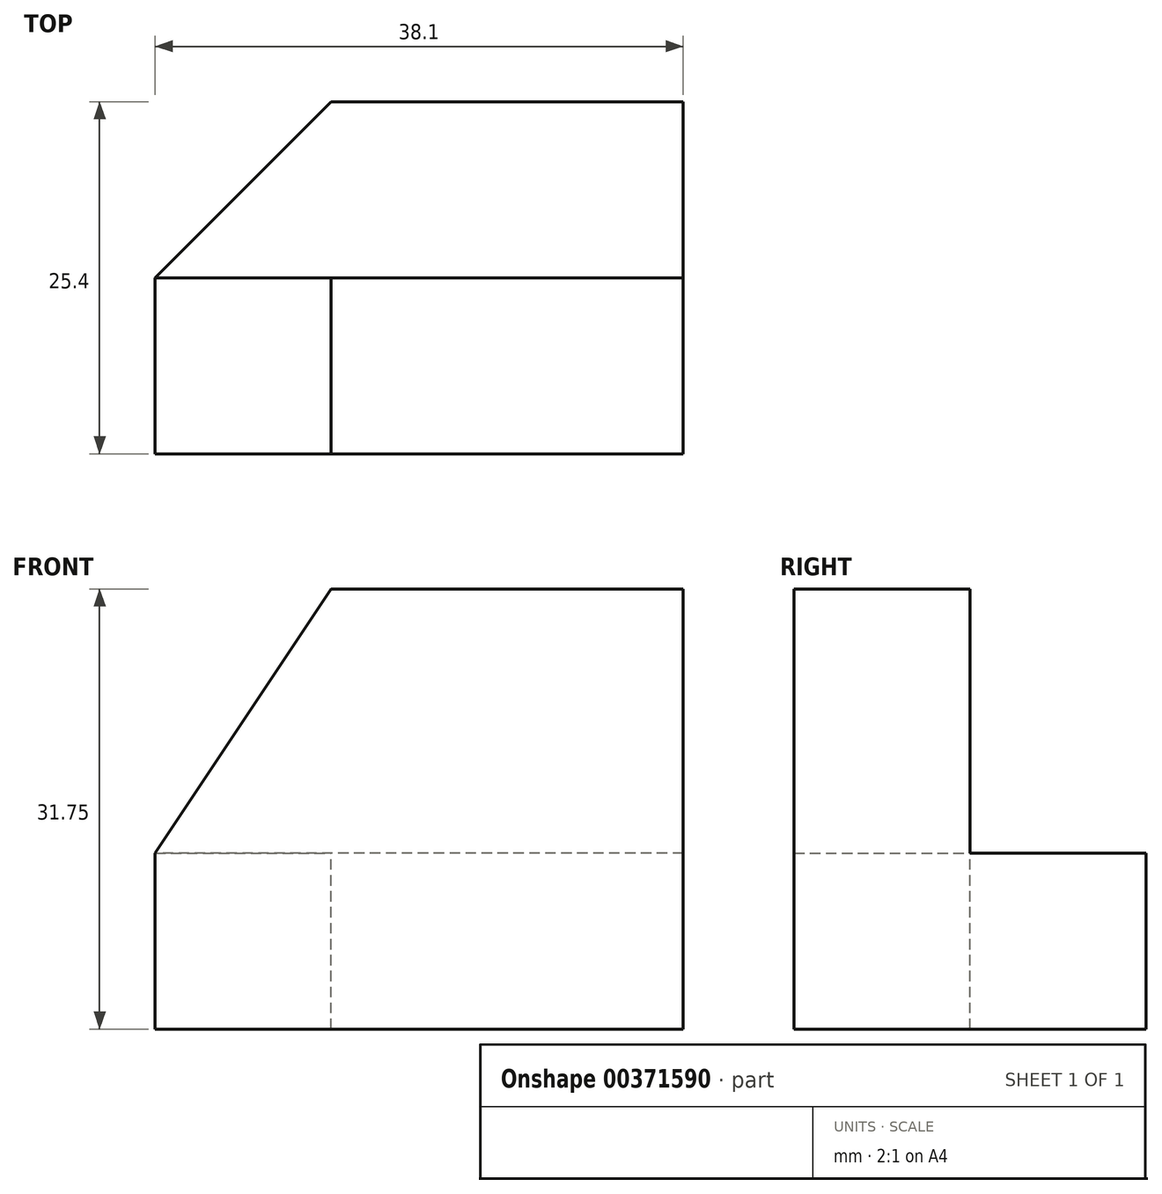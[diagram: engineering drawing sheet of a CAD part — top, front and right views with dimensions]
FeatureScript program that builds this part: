
annotation { "Feature Type Name" : "Feature", "Feature Type Description" : "" }
export const myFeature = defineFeature(function(context is Context, id is Id, definition is map)
    precondition{}
    {
        {
            var Q0;
            Q0=qCreatedBy(makeId("Right.planeOp"),FACE);
            var sketch = newSketch(context, id + "F0", { "sketchPlane" : qUnion([Q0])});
            skLineSegment(sketch, "E0.bottom", {"start": v(0, 0) * mm, "end": v(25.4, 0) * mm});
            skLineSegment(sketch, "E0.top", {"start": v(0, 31.75) * mm, "end": v(25.4, 31.75) * mm});
            skLineSegment(sketch, "E0.left", {"start": v(0, 0) * mm, "end": v(0, 31.75) * mm});
            skLineSegment(sketch, "E0.right", {"start": v(25.4, 0) * mm, "end": v(25.4, 31.75) * mm});
            skSolve(sketch);
        }
        {
            var Q0;
            Q0 = qSketchRegion(id + "F0", true);
            extrude(context, id + "F1", {"entities" : qUnion([Q0]), "depth" : 38.1 * mm});
        }
        {
            var Q0;
            Q0=makeQuery(id+"F1.opExtrude","CAP_FACE",FACE,{"disambiguationData":[OSD([sQuery(id+"F0.wireOp",EDGE,"E0.bottom"),sQuery(id+"F0.wireOp",EDGE,"E0.top"),sQuery(id+"F0.wireOp",EDGE,"E0.left"),sQuery(id+"F0.wireOp",EDGE,"E0.right")])],"isStart":true});
            var sketch = newSketch(context, id + "F2", { "sketchPlane" : qUnion([Q0])});
            skLineSegment(sketch, "E1", {"start": v(-12.7, 31.75) * mm, "end": v(-12.7, 12.7) * mm});
            skLineSegment(sketch, "E2", {"start": v(-12.7, 12.7) * mm, "end": v(-25.4, 12.7) * mm});
            skSolve(sketch);
        }
        {
            var Q0;
            {var subQ0=sQuery(id+"F2.wireOp",EDGE,"E1");Q0=makeQuery(id+"F2.imprint","IMPRINT",FACE,{"disambiguationData":[TD([[makeQuery(id+"F2.imprint","IMPRINT",EDGE,{"derivedFrom":subQ0}),-1.0]])]});}
            extrude(context, id + "F3", {"entities" : qUnion([Q0]), "operationType" : NewBodyOperationType.REMOVE, "oppositeDirection" : true, "depth" : 38.1 * mm});
        }
        {
            var Q0;
            Q0=makeQuery(id+"F3.boolean.opBoolean","COPY",FACE,{"derivedFrom":makeQuery(id+"F3.opExtrude","SWEPT_FACE",FACE,{"disambiguationData":[OSD([sQuery(id+"F2.wireOp",EDGE,"E1")])]})});
            var sketch = newSketch(context, id + "F4", { "sketchPlane" : qUnion([Q0])});
            skLineSegment(sketch, "E3", {"start": v(-12.7, 31.75) * mm, "end": v(0, 12.7) * mm});
            skSolve(sketch);
        }
        {
            var Q0;
            {var subQ0=sQuery(id+"F4.wireOp",EDGE,"E3");Q0=makeQuery(id+"F4.imprint","IMPRINT",FACE,{"disambiguationData":[TD([[makeQuery(id+"F4.imprint","IMPRINT",EDGE,{"derivedFrom":subQ0}),1.0]])]});}
            extrude(context, id + "F5", {"entities" : qUnion([Q0]), "operationType" : NewBodyOperationType.REMOVE, "oppositeDirection" : true, "depth" : 25.4 * mm});
        }
        {
            var Q0;
            Q0=makeQuery(id+"F3.boolean.opBoolean","COPY",FACE,{"derivedFrom":makeQuery(id+"F3.opExtrude","SWEPT_FACE",FACE,{"disambiguationData":[OSD([sQuery(id+"F2.wireOp",EDGE,"E2")])]})});
            var sketch = newSketch(context, id + "F6", { "sketchPlane" : qUnion([Q0])});
            skLineSegment(sketch, "E4", {"start": v(0, 12.7) * mm, "end": v(12.7, 25.4) * mm});
            skSolve(sketch);
        }
        {
            var Q0;
            {var subQ0=sQuery(id+"F6.wireOp",EDGE,"E4");Q0=makeQuery(id+"F6.imprint","IMPRINT",FACE,{"disambiguationData":[TD([[makeQuery(id+"F6.imprint","IMPRINT",EDGE,{"derivedFrom":subQ0}),1.0]])]});}
            extrude(context, id + "F7", {"entities" : qUnion([Q0]), "operationType" : NewBodyOperationType.REMOVE, "oppositeDirection" : true, "depth" : 25.4 * mm});
        }
    });
